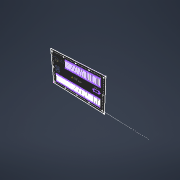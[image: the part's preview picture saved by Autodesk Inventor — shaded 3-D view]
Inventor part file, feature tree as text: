
AUTODESK INVENTOR PART (.ipt)
format: ipt  version: 2022 (Build 260153000, 153)  size: 1,932,288 bytes
history: native  units: mm
features: other x2, extrude x2, sketch x1
ambient origin geometry x8: Origin, YZ Plane, XZ Plane, XY Plane, X Axis, Y Axis, Z Axis, Center Point
feature tree (5):
  other  "РабПлоскость5"
  sketch  "Эскиз1"
  extrude  "Выдавливание2"  Depth=156.0mm
  extrude  "Выдавливание3"  Depth=2.0mm
  other  "Картинка4"
